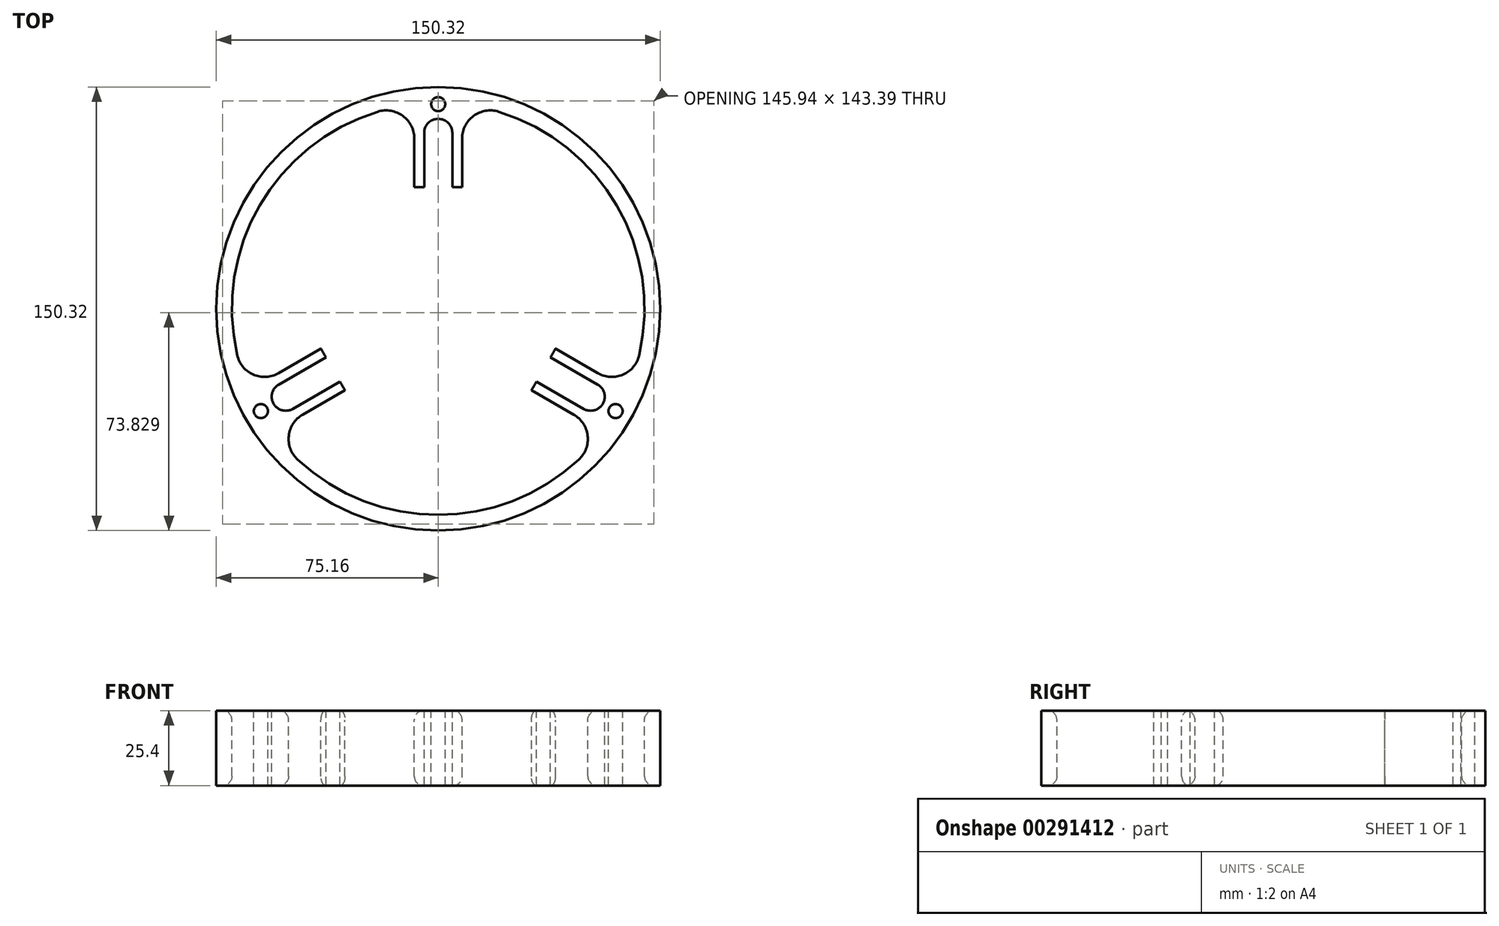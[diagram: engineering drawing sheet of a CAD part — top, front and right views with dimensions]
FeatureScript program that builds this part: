
annotation { "Feature Type Name" : "Feature", "Feature Type Description" : "" }
export const myFeature = defineFeature(function(context is Context, id is Id, definition is map)
    precondition{}
    {
        {
            var Q0;
            Q0=qCreatedBy(makeId("Top.planeOp"),FACE);
            var sketch = newSketch(context, id + "F0", { "sketchPlane" : qUnion([Q0])});
            skCircle(sketch, "E0", {"center": v(0, 0) * mm, "radius": 75.16 * mm});
            skArc(sketch, "E1", {"start": v(-20.43, 66.8) * mm, "mid": v(-60.5, 34.92) * mm, "end": v(-68.06, -15.7) * mm});
            skLineSegment(sketch, "E2", {"start": v(-8.12, 57.69) * mm, "end": v(-8.12, 41.15) * mm});
            skLineSegment(sketch, "E3", {"start": v(8.12, 57.69) * mm, "end": v(8.12, 41.15) * mm});
            skLineSegment(sketch, "E4.0", {"start": v(4.76, 59.59) * mm, "end": v(4.76, 41.15) * mm});
            skLineSegment(sketch, "E5.0", {"start": v(-4.76, 59.59) * mm, "end": v(-4.76, 41.15) * mm});
            skLineSegment(sketch, "E6", {"start": v(-8.12, 41.15) * mm, "end": v(-4.76, 41.15) * mm});
            skLineSegment(sketch, "E7", {"start": v(4.76, 41.15) * mm, "end": v(8.12, 41.15) * mm});
            skArc(sketch, "E8", {"start": v(4.76, 59.59) * mm, "mid": v(0, 64.35) * mm, "end": v(-4.76, 59.59) * mm});
            skPoint(sketch, "E9.visualSharp", {"position": v(8.12, 69.38) * mm});
            skArc(sketch, "E9.filletArc", {"start": v(20.43, 66.8) * mm, "mid": v(11.97, 65.35) * mm, "end": v(8.12, 57.69) * mm});
            skPoint(sketch, "E10.visualSharp", {"position": v(-8.12, 69.38) * mm});
            skArc(sketch, "E10.filletArc", {"start": v(-8.12, 57.69) * mm, "mid": v(-11.97, 65.35) * mm, "end": v(-20.43, 66.8) * mm});
            skArc(sketch, "E11.1.0", {"start": v(-45.9, -35.87) * mm, "mid": v(-50.6, -43.04) * mm, "end": v(-47.63, -51.09) * mm});
            skLineSegment(sketch, "E11.1.1", {"start": v(-45.9, -35.87) * mm, "end": v(-31.58, -27.6) * mm});
            skLineSegment(sketch, "E11.1.2", {"start": v(-31.58, -27.6) * mm, "end": v(-33.25, -24.7) * mm});
            skLineSegment(sketch, "E11.1.3", {"start": v(-49.22, -33.92) * mm, "end": v(-33.25, -24.7) * mm});
            skArc(sketch, "E11.1.4", {"start": v(-53.99, -25.67) * mm, "mid": v(-55.73, -32.18) * mm, "end": v(-49.22, -33.92) * mm});
            skLineSegment(sketch, "E11.1.5", {"start": v(-53.99, -25.67) * mm, "end": v(-38.02, -16.45) * mm});
            skLineSegment(sketch, "E11.1.6", {"start": v(-54.02, -21.82) * mm, "end": v(-39.7, -13.55) * mm});
            skArc(sketch, "E11.1.7", {"start": v(-68.06, -15.7) * mm, "mid": v(-62.58, -22.3) * mm, "end": v(-54.02, -21.82) * mm});
            skLineSegment(sketch, "E11.1.8", {"start": v(-38.02, -16.45) * mm, "end": v(-39.7, -13.55) * mm});
            skArc(sketch, "E11.2.0", {"start": v(54.02, -21.82) * mm, "mid": v(62.58, -22.3) * mm, "end": v(68.06, -15.7) * mm});
            skLineSegment(sketch, "E11.2.1", {"start": v(54.02, -21.82) * mm, "end": v(39.7, -13.55) * mm});
            skLineSegment(sketch, "E11.2.2", {"start": v(39.7, -13.55) * mm, "end": v(38.02, -16.45) * mm});
            skLineSegment(sketch, "E11.2.3", {"start": v(53.99, -25.67) * mm, "end": v(38.02, -16.45) * mm});
            skArc(sketch, "E11.2.4", {"start": v(49.22, -33.92) * mm, "mid": v(55.73, -32.18) * mm, "end": v(53.99, -25.67) * mm});
            skLineSegment(sketch, "E11.2.5", {"start": v(49.22, -33.92) * mm, "end": v(33.25, -24.7) * mm});
            skLineSegment(sketch, "E11.2.6", {"start": v(45.9, -35.87) * mm, "end": v(31.58, -27.6) * mm});
            skArc(sketch, "E11.2.7", {"start": v(47.63, -51.09) * mm, "mid": v(50.6, -43.04) * mm, "end": v(45.9, -35.87) * mm});
            skLineSegment(sketch, "E11.2.8", {"start": v(33.25, -24.7) * mm, "end": v(31.58, -27.6) * mm});
            skArc(sketch, "E12.trimOffspring", {"start": v(-47.63, -51.09) * mm, "mid": v(0, -69.85) * mm, "end": v(47.63, -51.09) * mm});
            skArc(sketch, "E13.trimOffspring", {"start": v(68.06, -15.7) * mm, "mid": v(60.5, 34.92) * mm, "end": v(20.43, 66.8) * mm});
            skCircle(sketch, "E14", {"center": v(0, 69.34) * mm, "radius": 2.38 * mm});
            skCircle(sketch, "E15.1.0", {"center": v(-60.05, -34.67) * mm, "radius": 2.38 * mm});
            skCircle(sketch, "E15.2.0", {"center": v(60.05, -34.67) * mm, "radius": 2.38 * mm});
            skSolve(sketch);
        }
        {
            var Q0;
            Q0 = qSketchRegion(id + "F0", true);
            extrude(context, id + "F1", {"entities" : qUnion([Q0]), "oppositeDirection" : true, "depth" : 25.4 * mm});
        }
        {
            var Q0;
            Q0=makeQuery(id+"F1.opExtrude","CAP_EDGE",EDGE,{"disambiguationData":[OSD([sQuery(id+"F0.wireOp",EDGE,"E1")])],"isStart":true});
            var Q1;
            Q1=makeQuery(id+"F1.opExtrude","CAP_EDGE",EDGE,{"disambiguationData":[OSD([sQuery(id+"F0.wireOp",EDGE,"E9.filletArc")])],"isStart":true});
            var Q2;
            Q2=makeQuery(id+"F1.opExtrude","CAP_EDGE",EDGE,{"disambiguationData":[OSD([sQuery(id+"F0.wireOp",EDGE,"E12.trimOffspring")])],"isStart":true});
            var Q3;
            Q3=makeQuery(id+"F1.opExtrude","CAP_EDGE",EDGE,{"disambiguationData":[OSD([sQuery(id+"F0.wireOp",EDGE,"E1")])],"isStart":false});
            var Q4;
            Q4=makeQuery(id+"F1.opExtrude","CAP_EDGE",EDGE,{"disambiguationData":[OSD([sQuery(id+"F0.wireOp",EDGE,"E12.trimOffspring")])],"isStart":false});
            var Q5;
            Q5=makeQuery(id+"F1.opExtrude","CAP_EDGE",EDGE,{"disambiguationData":[OSD([sQuery(id+"F0.wireOp",EDGE,"E13.trimOffspring")])],"isStart":false});
            fillet(context, id + "F2", {"entities" : qUnion([Q0, Q1, Q2, Q3, Q4, Q5]), "radius" : 3.17 * mm, "tangentPropagation" : true, "allowEdgeOverflow" : false});
        }
    });
